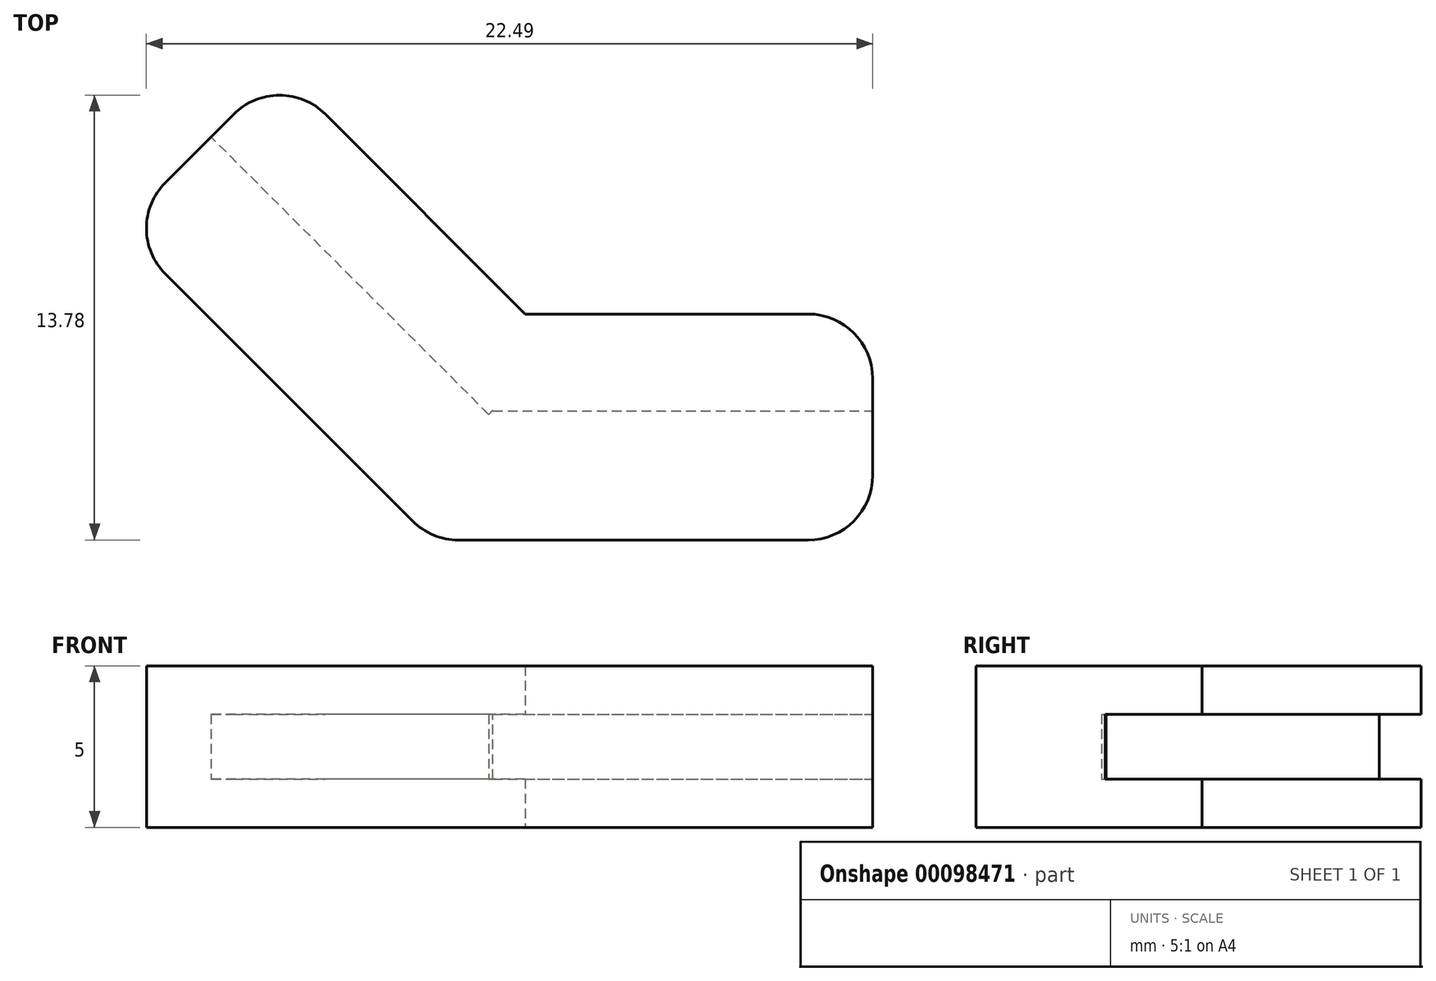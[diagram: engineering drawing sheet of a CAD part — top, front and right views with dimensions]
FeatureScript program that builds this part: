
annotation { "Feature Type Name" : "Feature", "Feature Type Description" : "" }
export const myFeature = defineFeature(function(context is Context, id is Id, definition is map)
    precondition{}
    {
        {
            var Q0;
            Q0=qCreatedBy(makeId("Top.planeOp"),FACE);
            var sketch = newSketch(context, id + "F0", { "sketchPlane" : qUnion([Q0])});
            skLineSegment(sketch, "E0", {"start": v(0, 0) * mm, "end": v(12, 0) * mm, "construction": true});
            skLineSegment(sketch, "E1", {"start": v(0, 0) * mm, "end": v(-8.49, 8.49) * mm, "construction": true});
            skLineSegment(sketch, "E2.0", {"start": v(-1.66, -4) * mm, "end": v(-11.31, 5.66) * mm});
            skLineSegment(sketch, "E2.1", {"start": v(-1.66, -4) * mm, "end": v(12, -4) * mm});
            skLineSegment(sketch, "E3.0", {"start": v(1.24, 3) * mm, "end": v(-6.36, 10.6) * mm});
            skLineSegment(sketch, "E3.1", {"start": v(1.24, 3) * mm, "end": v(12, 3) * mm});
            skLineSegment(sketch, "E4", {"start": v(-11.31, 5.66) * mm, "end": v(-6.36, 10.6) * mm});
            skLineSegment(sketch, "E5", {"start": v(12, -4) * mm, "end": v(12, 3) * mm});
            skSolve(sketch);
        }
        {
            var Q0;
            Q0 = qSketchRegion(id + "F0", true);
            extrude(context, id + "F1", {"entities" : qUnion([Q0]), "depth" : 5 * mm});
        }
        {
            var Q0;
            Q0=makeQuery(id+"F1.opExtrude","SWEPT_FACE",FACE,{"disambiguationData":[OSD([sQuery(id+"F0.wireOp",EDGE,"E3.0")])]});
            var sketch = newSketch(context, id + "F2", { "sketchPlane" : qUnion([Q0])});
            skLineSegment(sketch, "E6", {"start": v(12, 2.5) * mm, "end": v(1.24, 2.5) * mm, "construction": true});
            skLineSegment(sketch, "E7.bottom", {"start": v(1.24, 3.5) * mm, "end": v(12, 3.5) * mm});
            skLineSegment(sketch, "E7.top", {"start": v(1.24, 1.5) * mm, "end": v(12, 1.5) * mm});
            skLineSegment(sketch, "E7.right", {"start": v(12, 3.5) * mm, "end": v(12, 1.5) * mm});
            skPoint(sketch, "E7.middle", {"position": v(6.62, 2.5) * mm});
            skLineSegment(sketch, "E8", {"start": v(1.24, 1.5) * mm, "end": v(1.24, 1.5) * mm});
            skLineSegment(sketch, "E9", {"start": v(1.24, 1.5) * mm, "end": v(1.24, 3.5) * mm});
            skLineSegment(sketch, "E10", {"start": v(1.24, 3.5) * mm, "end": v(1.24, 3.5) * mm});
            skSolve(sketch);
        }
        {
            var Q0;
            Q0 = qSketchRegion(id + "F2", true);
            extrude(context, id + "F3", {"entities" : qUnion([Q0]), "operationType" : NewBodyOperationType.REMOVE, "oppositeDirection" : true, "depth" : 3 * mm});
        }
        {
            var Q0;
            Q0=makeQuery(id+"F1.opExtrude","SWEPT_FACE",FACE,{"disambiguationData":[OSD([sQuery(id+"F0.wireOp",EDGE,"E3.1")])]});
            var sketch = newSketch(context, id + "F4", { "sketchPlane" : qUnion([Q0])});
            skLineSegment(sketch, "E11", {"start": v(-1.24, 2.5) * mm, "end": v(-12, 2.5) * mm, "construction": true});
            skLineSegment(sketch, "E12.bottom", {"start": v(-1.24, 3.5) * mm, "end": v(-12, 3.5) * mm});
            skLineSegment(sketch, "E12.top", {"start": v(-1.24, 1.5) * mm, "end": v(-12, 1.5) * mm});
            skLineSegment(sketch, "E12.left", {"start": v(-1.24, 3.5) * mm, "end": v(-1.24, 1.5) * mm});
            skLineSegment(sketch, "E12.right", {"start": v(-12, 3.5) * mm, "end": v(-12, 1.5) * mm});
            skSolve(sketch);
        }
        {
            var Q0;
            Q0 = qSketchRegion(id + "F4", true);
            extrude(context, id + "F5", {"entities" : qUnion([Q0]), "operationType" : NewBodyOperationType.REMOVE, "oppositeDirection" : true, "depth" : 3 * mm});
        }
        {
            var Q0;
            Q0=makeQuery(id+"F5.boolean.opBoolean","COPY",FACE,{"derivedFrom":makeQuery(id+"F5.opExtrude","SWEPT_FACE",FACE,{"disambiguationData":[OSD([sQuery(id+"F4.wireOp",EDGE,"E12.left")])]})});
            var sketch = newSketch(context, id + "F6", { "sketchPlane" : qUnion([Q0])});
            skLineSegment(sketch, "E13.0", {"start": v(3, 3.5) * mm, "end": v(3, 1.5) * mm});
            skLineSegment(sketch, "E13.1", {"start": v(0, 1.5) * mm, "end": v(3, 1.5) * mm});
            skLineSegment(sketch, "E13.2", {"start": v(0, 3.5) * mm, "end": v(3, 3.5) * mm});
            skLineSegment(sketch, "E13.3", {"start": v(0, 3.5) * mm, "end": v(0, 1.5) * mm});
            skSolve(sketch);
        }
        {
            var Q0;
            Q0 = qSketchRegion(id + "F6", true);
            extrude(context, id + "F7", {"entities" : qUnion([Q0]), "operationType" : NewBodyOperationType.REMOVE, "oppositeDirection" : true, "depth" : 1 * mm});
        }
        {
            var Q0;
            Q0=makeQuery(id+"F3.boolean.opBoolean","COPY",FACE,{"derivedFrom":makeQuery(id+"F3.opExtrude","SWEPT_FACE",FACE,{"disambiguationData":[OSD([sQuery(id+"F2.wireOp",EDGE,"E9")])]})});
            var sketch = newSketch(context, id + "F8", { "sketchPlane" : qUnion([Q0])});
            skLineSegment(sketch, "E14.0", {"start": v(0, 3.5) * mm, "end": v(0, 1.5) * mm});
            skLineSegment(sketch, "E14.1", {"start": v(0, 1.5) * mm, "end": v(-1.59, 1.5) * mm});
            skLineSegment(sketch, "E14.2", {"start": v(-1.59, 1.5) * mm, "end": v(-1.59, 3.5) * mm});
            skLineSegment(sketch, "E14.3", {"start": v(0, 3.5) * mm, "end": v(-1.59, 3.5) * mm});
            skPoint(sketch, "E15.orphan", {"position": v(-3, 1.5) * mm});
            skPoint(sketch, "E16.orphan", {"position": v(-3, 3.5) * mm});
            skSolve(sketch);
        }
        {
            var Q0;
            Q0 = qSketchRegion(id + "F8", true);
            extrude(context, id + "F9", {"entities" : qUnion([Q0]), "operationType" : NewBodyOperationType.REMOVE, "oppositeDirection" : true, "depth" : 1.4 * mm});
        }
        {
            var Q0;
            Q0=makeQuery(id+"F1.opExtrude","SWEPT_EDGE",EDGE,{"disambiguationData":[OSD([sQuery(id+"F0.wireOp",EDGE,"E2.0"),sQuery(id+"F0.wireOp",EDGE,"E2.1")])]});
            var Q1;
            Q1=makeQuery(id+"F1.opExtrude","SWEPT_EDGE",EDGE,{"disambiguationData":[OSD([sQuery(id+"F0.wireOp",EDGE,"E2.0"),sQuery(id+"F0.wireOp",EDGE,"E4")])]});
            var Q2;
            Q2=makeQuery(id+"F1.opExtrude","SWEPT_EDGE",EDGE,{"disambiguationData":[OSD([sQuery(id+"F0.wireOp",EDGE,"E2.1"),sQuery(id+"F0.wireOp",EDGE,"E5")])]});
            var Q3;
            {var subQ0=sQuery(id+"F0.wireOp",EDGE,"E5");var subQ1=sQuery(id+"F0.wireOp",EDGE,"E3.1");Q3=makeQuery(id+"F5.boolean.opBoolean","SPLIT",EDGE,{"disambiguationData":[TD([makeQuery(id+"F5.opExtrude","SWEPT_FACE",FACE,{"disambiguationData":[OSD([sQuery(id+"F4.wireOp",EDGE,"E12.bottom")])]})])],"derivedFrom":makeQuery(id+"F1.opExtrude","SWEPT_EDGE",EDGE,{"disambiguationData":[OSD([subQ1,subQ0])]})});}
            var Q4;
            {var subQ0=sQuery(id+"F0.wireOp",EDGE,"E5");var subQ1=sQuery(id+"F0.wireOp",EDGE,"E3.1");Q4=makeQuery(id+"F5.boolean.opBoolean","SPLIT",EDGE,{"disambiguationData":[TD([makeQuery(id+"F5.opExtrude","SWEPT_FACE",FACE,{"disambiguationData":[OSD([sQuery(id+"F4.wireOp",EDGE,"E12.top")])]})])],"derivedFrom":makeQuery(id+"F1.opExtrude","SWEPT_EDGE",EDGE,{"disambiguationData":[OSD([subQ1,subQ0])]})});}
            var Q5;
            {var subQ0=sQuery(id+"F0.wireOp",EDGE,"E4");var subQ1=sQuery(id+"F0.wireOp",EDGE,"E3.0");Q5=makeQuery(id+"F3.boolean.opBoolean","SPLIT",EDGE,{"disambiguationData":[TD([makeQuery(id+"F3.opExtrude","SWEPT_FACE",FACE,{"disambiguationData":[OSD([sQuery(id+"F2.wireOp",EDGE,"E7.bottom")])]})])],"derivedFrom":makeQuery(id+"F1.opExtrude","SWEPT_EDGE",EDGE,{"disambiguationData":[OSD([subQ1,subQ0])]})});}
            var Q6;
            {var subQ0=sQuery(id+"F0.wireOp",EDGE,"E4");var subQ1=sQuery(id+"F0.wireOp",EDGE,"E3.0");Q6=makeQuery(id+"F3.boolean.opBoolean","SPLIT",EDGE,{"disambiguationData":[TD([makeQuery(id+"F3.opExtrude","SWEPT_FACE",FACE,{"disambiguationData":[OSD([sQuery(id+"F2.wireOp",EDGE,"E7.top")])]})])],"derivedFrom":makeQuery(id+"F1.opExtrude","SWEPT_EDGE",EDGE,{"disambiguationData":[OSD([subQ1,subQ0])]})});}
            fillet(context, id + "F10", {"entities" : qUnion([Q0, Q1, Q2, Q3, Q4, Q5, Q6]), "radius" : 2 * mm, "tangentPropagation" : true, "allowEdgeOverflow" : false});
        }
    });
